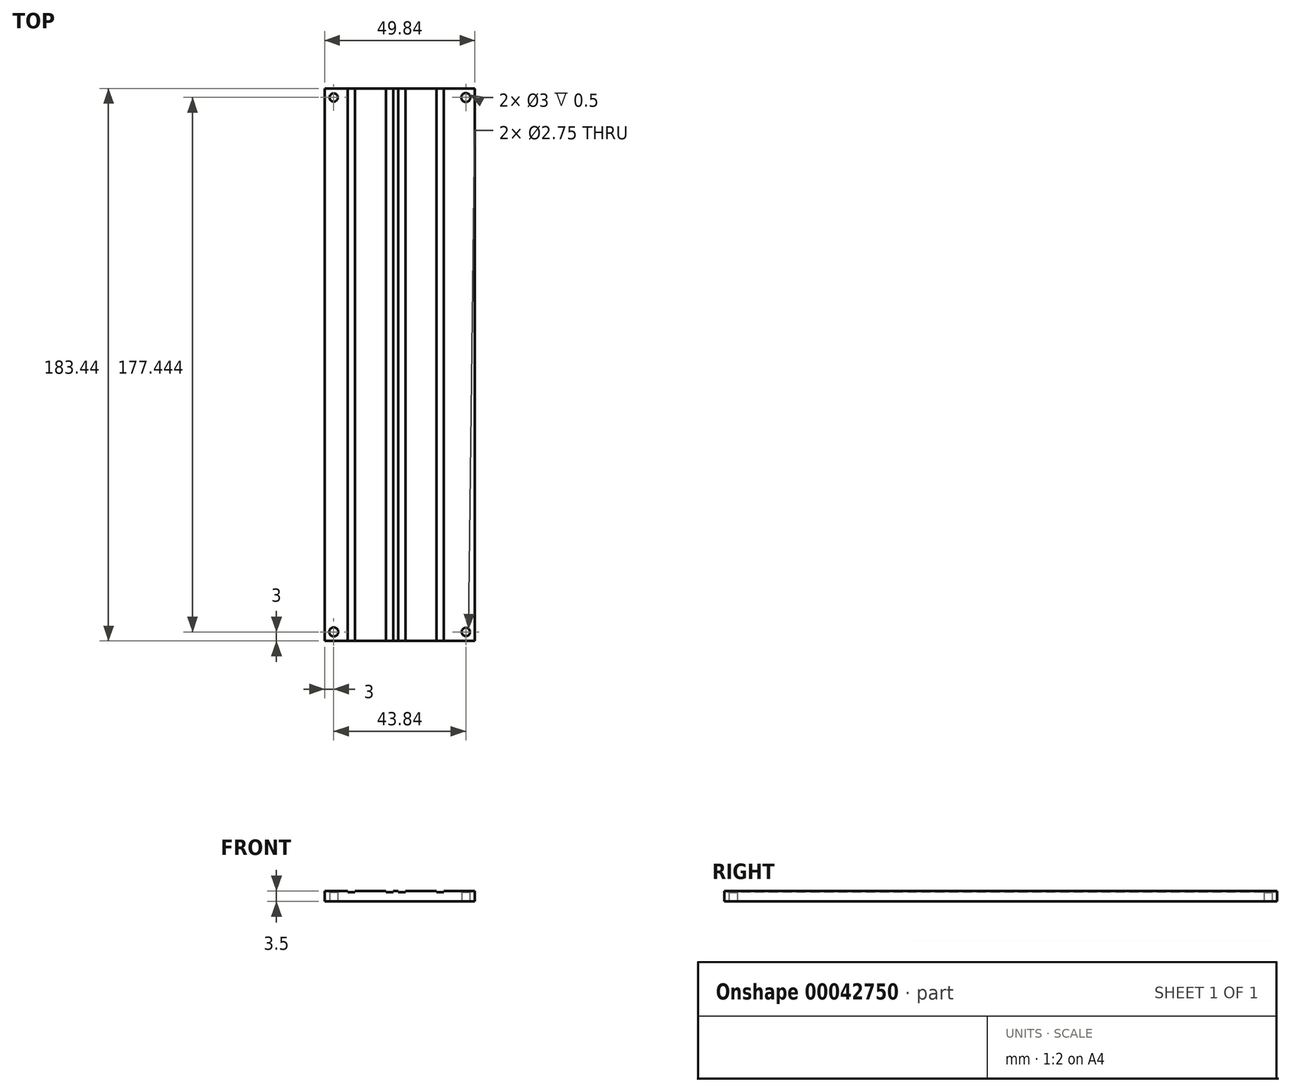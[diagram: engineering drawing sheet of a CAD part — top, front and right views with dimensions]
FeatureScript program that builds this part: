
annotation { "Feature Type Name" : "Feature", "Feature Type Description" : "" }
export const myFeature = defineFeature(function(context is Context, id is Id, definition is map)
    precondition{}
    {
        {
            var Q0;
            Q0=qCreatedBy(makeId("Top.planeOp"),FACE);
            var sketch = newSketch(context, id + "F0", { "sketchPlane" : qUnion([Q0])});
            skCircle(sketch, "E0", {"center": v(0, 0) * mm, "radius": 1.5 * mm});
            skCircle(sketch, "E1", {"center": v(43.84, 177.44) * mm, "radius": 1.5 * mm});
            skLineSegment(sketch, "E2.bottom", {"start": v(-3, 180.44) * mm, "end": v(46.84, 180.44) * mm});
            skLineSegment(sketch, "E2.top", {"start": v(-3, -3) * mm, "end": v(46.84, -3) * mm});
            skLineSegment(sketch, "E2.left", {"start": v(-3, 180.44) * mm, "end": v(-3, -3) * mm});
            skLineSegment(sketch, "E2.right", {"start": v(46.84, 180.44) * mm, "end": v(46.84, -3) * mm});
            skCircle(sketch, "E3", {"center": v(0, 177.44) * mm, "radius": 1.38 * mm});
            skCircle(sketch, "E4", {"center": v(43.84, 0) * mm, "radius": 1.38 * mm});
            skPoint(sketch, "E5.endSnap0", {"position": v(21.92, -3) * mm});
            skSolve(sketch);
        }
        {
            var Q0;
            Q0=makeQuery(id+"F0.imprint","IMPRINT",FACE,{"disambiguationData":[TD([[makeQuery(id+"F0.imprint","IMPRINT",EDGE,{"derivedFrom":sQuery(id+"F0.wireOp",EDGE,"E0")}),-1.0]])]});
            extrude(context, id + "F1", {"entities" : qUnion([Q0]), "depth" : .5 * mm});
        }
        {
            var Q0;
            Q0=makeQuery(id+"F1.opExtrude","CAP_FACE",FACE,{"disambiguationData":[OSD([sQuery(id+"F0.wireOp",EDGE,"E0"),sQuery(id+"F0.wireOp",EDGE,"E1"),sQuery(id+"F0.wireOp",EDGE,"E2.bottom"),sQuery(id+"F0.wireOp",EDGE,"E2.top"),sQuery(id+"F0.wireOp",EDGE,"E2.left"),sQuery(id+"F0.wireOp",EDGE,"E2.right"),sQuery(id+"F0.wireOp",EDGE,"e5278f3a-593b-43ce-a0b6-dc1b815632bb.rect.bottom"),sQuery(id+"F0.wireOp",EDGE,"e5278f3a-593b-43ce-a0b6-dc1b815632bb.rect.top"),sQuery(id+"F0.wireOp",EDGE,"e5278f3a-593b-43ce-a0b6-dc1b815632bb.rect.left"),sQuery(id+"F0.wireOp",EDGE,"e5278f3a-593b-43ce-a0b6-dc1b815632bb.rect.right"),sQuery(id+"F0.wireOp",EDGE,"0788b160-4dc1-422e-8e8c-0d42d97e9e21.rect.right"),sQuery(id+"F0.wireOp",EDGE,"0788b160-4dc1-422e-8e8c-0d42d97e9e21.rect.left"),sQuery(id+"F0.wireOp",EDGE,"0788b160-4dc1-422e-8e8c-0d42d97e9e21.rect.top"),sQuery(id+"F0.wireOp",EDGE,"0788b160-4dc1-422e-8e8c-0d42d97e9e21.rect.bottom"),sQuery(id+"F0.wireOp",EDGE,"9ae8423b-224c-4eed-8461-ac0ba12c67ef.rect.top"),sQuery(id+"F0.wireOp",EDGE,"9ae8423b-224c-4eed-8461-ac0ba12c67ef.rect.bottom"),sQuery(id+"F0.wireOp",EDGE,"9ae8423b-224c-4eed-8461-ac0ba12c67ef.rect.left"),sQuery(id+"F0.wireOp",EDGE,"9ae8423b-224c-4eed-8461-ac0ba12c67ef.rect.right"),sQuery(id+"F0.wireOp",EDGE,"511b1452-fdba-401d-9405-732c8af2f196.rect.top"),sQuery(id+"F0.wireOp",EDGE,"5224c5d0-f24c-45e1-9878-aebc782a1e99.rect.left"),sQuery(id+"F0.wireOp",EDGE,"511b1452-fdba-401d-9405-732c8af2f196.rect.bottom"),sQuery(id+"F0.wireOp",EDGE,"86b0135e-4755-4367-ae23-b1d375861a25.rect.top"),sQuery(id+"F0.wireOp",EDGE,"5224c5d0-f24c-45e1-9878-aebc782a1e99.rect.bottom"),sQuery(id+"F0.wireOp",EDGE,"5224c5d0-f24c-45e1-9878-aebc782a1e99.rect.top"),sQuery(id+"F0.wireOp",EDGE,"86b0135e-4755-4367-ae23-b1d375861a25.rect.bottom"),sQuery(id+"F0.wireOp",EDGE,"5224c5d0-f24c-45e1-9878-aebc782a1e99.rect.right"),sQuery(id+"F0.wireOp",EDGE,"86b0135e-4755-4367-ae23-b1d375861a25.rect.left"),sQuery(id+"F0.wireOp",EDGE,"86b0135e-4755-4367-ae23-b1d375861a25.rect.right"),sQuery(id+"F0.wireOp",EDGE,"511b1452-fdba-401d-9405-732c8af2f196.rect.right"),sQuery(id+"F0.wireOp",EDGE,"511b1452-fdba-401d-9405-732c8af2f196.rect.left"),sQuery(id+"F0.wireOp",EDGE,"b43a0ba4-9dba-46bc-968b-13e96fca23b3.rect.left"),sQuery(id+"F0.wireOp",EDGE,"b43a0ba4-9dba-46bc-968b-13e96fca23b3.rect.bottom"),sQuery(id+"F0.wireOp",EDGE,"7761b7ab-5946-4f6e-ad21-f6075cb1ff51.rect.top"),sQuery(id+"F0.wireOp",EDGE,"4726b28d-0386-4670-8967-bc6313adf6ef.rect.right"),sQuery(id+"F0.wireOp",EDGE,"7761b7ab-5946-4f6e-ad21-f6075cb1ff51.rect.right"),sQuery(id+"F0.wireOp",EDGE,"4726b28d-0386-4670-8967-bc6313adf6ef.rect.top"),sQuery(id+"F0.wireOp",EDGE,"b43a0ba4-9dba-46bc-968b-13e96fca23b3.rect.right"),sQuery(id+"F0.wireOp",EDGE,"4726b28d-0386-4670-8967-bc6313adf6ef.rect.bottom"),sQuery(id+"F0.wireOp",EDGE,"4726b28d-0386-4670-8967-bc6313adf6ef.rect.left"),sQuery(id+"F0.wireOp",EDGE,"7761b7ab-5946-4f6e-ad21-f6075cb1ff51.rect.left"),sQuery(id+"F0.wireOp",EDGE,"b43a0ba4-9dba-46bc-968b-13e96fca23b3.rect.top"),sQuery(id+"F0.wireOp",EDGE,"7761b7ab-5946-4f6e-ad21-f6075cb1ff51.rect.bottom"),sQuery(id+"F0.wireOp",EDGE,"57ca4f26-5c56-4c68-9457-4a64392f3347.rect.left"),sQuery(id+"F0.wireOp",EDGE,"0ff1be2a-a1a8-4b6e-9f00-62856e441f21.rect.right"),sQuery(id+"F0.wireOp",EDGE,"208a584b-ce05-4589-bfe7-39b1698a8194.rect.left"),sQuery(id+"F0.wireOp",EDGE,"3fd6ee33-8733-46eb-a767-dbbe76983c7d.rect.left"),sQuery(id+"F0.wireOp",EDGE,"7a9b5616-fe8a-4a4b-9298-42c4a7e55be2.rect.right"),sQuery(id+"F0.wireOp",EDGE,"04949f4e-e150-414f-b18a-4da78bc3358c.rect.right"),sQuery(id+"F0.wireOp",EDGE,"208a584b-ce05-4589-bfe7-39b1698a8194.rect.right"),sQuery(id+"F0.wireOp",EDGE,"7a9b5616-fe8a-4a4b-9298-42c4a7e55be2.rect.left"),sQuery(id+"F0.wireOp",EDGE,"3fd6ee33-8733-46eb-a767-dbbe76983c7d.rect.right"),sQuery(id+"F0.wireOp",EDGE,"04949f4e-e150-414f-b18a-4da78bc3358c.rect.left"),sQuery(id+"F0.wireOp",EDGE,"57ca4f26-5c56-4c68-9457-4a64392f3347.rect.right"),sQuery(id+"F0.wireOp",EDGE,"0ff1be2a-a1a8-4b6e-9f00-62856e441f21.rect.left"),sQuery(id+"F0.wireOp",EDGE,"04949f4e-e150-414f-b18a-4da78bc3358c.rect.top"),sQuery(id+"F0.wireOp",EDGE,"208a584b-ce05-4589-bfe7-39b1698a8194.rect.bottom"),sQuery(id+"F0.wireOp",EDGE,"7a9b5616-fe8a-4a4b-9298-42c4a7e55be2.rect.top"),sQuery(id+"F0.wireOp",EDGE,"208a584b-ce05-4589-bfe7-39b1698a8194.rect.top"),sQuery(id+"F0.wireOp",EDGE,"0ff1be2a-a1a8-4b6e-9f00-62856e441f21.rect.bottom"),sQuery(id+"F0.wireOp",EDGE,"7a9b5616-fe8a-4a4b-9298-42c4a7e55be2.rect.bottom"),sQuery(id+"F0.wireOp",EDGE,"0ff1be2a-a1a8-4b6e-9f00-62856e441f21.rect.top"),sQuery(id+"F0.wireOp",EDGE,"57ca4f26-5c56-4c68-9457-4a64392f3347.rect.top"),sQuery(id+"F0.wireOp",EDGE,"57ca4f26-5c56-4c68-9457-4a64392f3347.rect.bottom"),sQuery(id+"F0.wireOp",EDGE,"04949f4e-e150-414f-b18a-4da78bc3358c.rect.bottom"),sQuery(id+"F0.wireOp",EDGE,"3fd6ee33-8733-46eb-a767-dbbe76983c7d.rect.top"),sQuery(id+"F0.wireOp",EDGE,"3fd6ee33-8733-46eb-a767-dbbe76983c7d.rect.bottom"),sQuery(id+"F0.wireOp",EDGE,"e532b4a8-563d-4d6a-8b1a-a20fa318d2fc.rect.right"),sQuery(id+"F0.wireOp",EDGE,"70cd7b72-5c6a-41ce-aa97-58821a5495a2.rect.left"),sQuery(id+"F0.wireOp",EDGE,"c8e58609-f867-4bb0-9ef6-a67fd09ed313.rect.left"),sQuery(id+"F0.wireOp",EDGE,"7f84faf9-ebf7-483f-8f19-fe061d16c88f.rect.right"),sQuery(id+"F0.wireOp",EDGE,"7939643b-5da5-488a-aeaf-6eee9e5d4f94.rect.left"),sQuery(id+"F0.wireOp",EDGE,"32a260d1-513d-470c-9a95-00da4923ba82.rect.right"),sQuery(id+"F0.wireOp",EDGE,"88e53884-e192-42f0-bd1f-923dc15386a3.rect.right"),sQuery(id+"F0.wireOp",EDGE,"70cd7b72-5c6a-41ce-aa97-58821a5495a2.rect.right"),sQuery(id+"F0.wireOp",EDGE,"e532b4a8-563d-4d6a-8b1a-a20fa318d2fc.rect.left"),sQuery(id+"F0.wireOp",EDGE,"c8e58609-f867-4bb0-9ef6-a67fd09ed313.rect.right"),sQuery(id+"F0.wireOp",EDGE,"7f84faf9-ebf7-483f-8f19-fe061d16c88f.rect.left"),sQuery(id+"F0.wireOp",EDGE,"32a260d1-513d-470c-9a95-00da4923ba82.rect.left"),sQuery(id+"F0.wireOp",EDGE,"f61bf7cc-c32d-46f2-bc22-689eb20f4aa8.rect.right"),sQuery(id+"F0.wireOp",EDGE,"528fd60a-5173-460b-8718-95726cf1d0d3.rect.right"),sQuery(id+"F0.wireOp",EDGE,"7939643b-5da5-488a-aeaf-6eee9e5d4f94.rect.right"),sQuery(id+"F0.wireOp",EDGE,"88e53884-e192-42f0-bd1f-923dc15386a3.rect.left"),sQuery(id+"F0.wireOp",EDGE,"f61bf7cc-c32d-46f2-bc22-689eb20f4aa8.rect.left"),sQuery(id+"F0.wireOp",EDGE,"528fd60a-5173-460b-8718-95726cf1d0d3.rect.left"),sQuery(id+"F0.wireOp",EDGE,"601dbf1e-1562-48c8-971d-08c2e95b1b61.rect.left"),sQuery(id+"F0.wireOp",EDGE,"c8e58609-f867-4bb0-9ef6-a67fd09ed313.rect.bottom"),sQuery(id+"F0.wireOp",EDGE,"88e53884-e192-42f0-bd1f-923dc15386a3.rect.top"),sQuery(id+"F0.wireOp",EDGE,"70cd7b72-5c6a-41ce-aa97-58821a5495a2.rect.bottom"),sQuery(id+"F0.wireOp",EDGE,"75fc349b-8e82-414b-b9d7-0717b741608d.rect.right"),sQuery(id+"F0.wireOp",EDGE,"2ff48f1a-e787-4175-bc96-8065b9f0d86f.rect.top"),sQuery(id+"F0.wireOp",EDGE,"75fc349b-8e82-414b-b9d7-0717b741608d.rect.bottom"),sQuery(id+"F0.wireOp",EDGE,"2ff48f1a-e787-4175-bc96-8065b9f0d86f.rect.left"),sQuery(id+"F0.wireOp",EDGE,"2ff48f1a-e787-4175-bc96-8065b9f0d86f.rect.bottom"),sQuery(id+"F0.wireOp",EDGE,"32a260d1-513d-470c-9a95-00da4923ba82.rect.bottom"),sQuery(id+"F0.wireOp",EDGE,"88e53884-e192-42f0-bd1f-923dc15386a3.rect.bottom"),sQuery(id+"F0.wireOp",EDGE,"528fd60a-5173-460b-8718-95726cf1d0d3.rect.top"),sQuery(id+"F0.wireOp",EDGE,"f61bf7cc-c32d-46f2-bc22-689eb20f4aa8.rect.bottom"),sQuery(id+"F0.wireOp",EDGE,"601dbf1e-1562-48c8-971d-08c2e95b1b61.rect.right"),sQuery(id+"F0.wireOp",EDGE,"7f84faf9-ebf7-483f-8f19-fe061d16c88f.rect.top"),sQuery(id+"F0.wireOp",EDGE,"601dbf1e-1562-48c8-971d-08c2e95b1b61.rect.bottom"),sQuery(id+"F0.wireOp",EDGE,"528fd60a-5173-460b-8718-95726cf1d0d3.rect.bottom"),sQuery(id+"F0.wireOp",EDGE,"e532b4a8-563d-4d6a-8b1a-a20fa318d2fc.rect.top"),sQuery(id+"F0.wireOp",EDGE,"75fc349b-8e82-414b-b9d7-0717b741608d.rect.top"),sQuery(id+"F0.wireOp",EDGE,"601dbf1e-1562-48c8-971d-08c2e95b1b61.rect.top"),sQuery(id+"F0.wireOp",EDGE,"32a260d1-513d-470c-9a95-00da4923ba82.rect.top"),sQuery(id+"F0.wireOp",EDGE,"f61bf7cc-c32d-46f2-bc22-689eb20f4aa8.rect.top"),sQuery(id+"F0.wireOp",EDGE,"7f84faf9-ebf7-483f-8f19-fe061d16c88f.rect.bottom"),sQuery(id+"F0.wireOp",EDGE,"e532b4a8-563d-4d6a-8b1a-a20fa318d2fc.rect.bottom"),sQuery(id+"F0.wireOp",EDGE,"70cd7b72-5c6a-41ce-aa97-58821a5495a2.rect.top"),sQuery(id+"F0.wireOp",EDGE,"75fc349b-8e82-414b-b9d7-0717b741608d.rect.left"),sQuery(id+"F0.wireOp",EDGE,"7939643b-5da5-488a-aeaf-6eee9e5d4f94.rect.bottom"),sQuery(id+"F0.wireOp",EDGE,"7939643b-5da5-488a-aeaf-6eee9e5d4f94.rect.top"),sQuery(id+"F0.wireOp",EDGE,"c8e58609-f867-4bb0-9ef6-a67fd09ed313.rect.top"),sQuery(id+"F0.wireOp",EDGE,"2ff48f1a-e787-4175-bc96-8065b9f0d86f.rect.right"),sQuery(id+"F0.wireOp",EDGE,"34bcf3fd-ed4a-4185-adf8-dc405735c649.rect.left"),sQuery(id+"F0.wireOp",EDGE,"e34a8003-39e3-4020-9972-05b17e0e0dd2.rect.right"),sQuery(id+"F0.wireOp",EDGE,"5d584f02-6df5-43d9-a6c0-44b15491b2ef.rect.right"),sQuery(id+"F0.wireOp",EDGE,"5d584f02-6df5-43d9-a6c0-44b15491b2ef.rect.left"),sQuery(id+"F0.wireOp",EDGE,"34bcf3fd-ed4a-4185-adf8-dc405735c649.rect.right"),sQuery(id+"F0.wireOp",EDGE,"e34a8003-39e3-4020-9972-05b17e0e0dd2.rect.left"),sQuery(id+"F0.wireOp",EDGE,"5d584f02-6df5-43d9-a6c0-44b15491b2ef.rect.bottom"),sQuery(id+"F0.wireOp",EDGE,"e34a8003-39e3-4020-9972-05b17e0e0dd2.rect.top"),sQuery(id+"F0.wireOp",EDGE,"e34a8003-39e3-4020-9972-05b17e0e0dd2.rect.bottom"),sQuery(id+"F0.wireOp",EDGE,"34bcf3fd-ed4a-4185-adf8-dc405735c649.rect.bottom"),sQuery(id+"F0.wireOp",EDGE,"34bcf3fd-ed4a-4185-adf8-dc405735c649.rect.top"),sQuery(id+"F0.wireOp",EDGE,"5d584f02-6df5-43d9-a6c0-44b15491b2ef.rect.top"),sQuery(id+"F0.wireOp",EDGE,"af60b362-f3e8-441e-9e1f-4259201feecf.rect.top"),sQuery(id+"F0.wireOp",EDGE,"f3d3602e-e124-40a7-96a1-dc4fa4adcf37.rect.bottom"),sQuery(id+"F0.wireOp",EDGE,"4a09bc43-db4a-4a7f-b510-9db42ac8ae9a.rect.top"),sQuery(id+"F0.wireOp",EDGE,"74e83cdb-cc94-4001-ac12-18727aacc957.rect.bottom"),sQuery(id+"F0.wireOp",EDGE,"242bfa70-7804-440d-99c3-28ec5b1ee65b.rect.left"),sQuery(id+"F0.wireOp",EDGE,"52d42c98-a837-46c3-ad31-eb32c8073d4f.rect.bottom"),sQuery(id+"F0.wireOp",EDGE,"af60b362-f3e8-441e-9e1f-4259201feecf.rect.left"),sQuery(id+"F0.wireOp",EDGE,"9a44f7b1-bce2-4215-bd6e-a2994b21c9db.rect.left"),sQuery(id+"F0.wireOp",EDGE,"9a44f7b1-bce2-4215-bd6e-a2994b21c9db.rect.top"),sQuery(id+"F0.wireOp",EDGE,"8898d686-7fb0-4204-8ff5-b49aa4418833.rect.bottom"),sQuery(id+"F0.wireOp",EDGE,"af60b362-f3e8-441e-9e1f-4259201feecf.rect.bottom"),sQuery(id+"F0.wireOp",EDGE,"47ae59bc-59bf-44a3-84ce-727988fe69e2.rect.top"),sQuery(id+"F0.wireOp",EDGE,"bc846ad1-a97c-4f09-9111-d1a515cad6f8.rect.bottom"),sQuery(id+"F0.wireOp",EDGE,"4a09bc43-db4a-4a7f-b510-9db42ac8ae9a.rect.right"),sQuery(id+"F0.wireOp",EDGE,"c0278d55-c928-4a3d-bbfd-8237f96a4b24.rect.top"),sQuery(id+"F0.wireOp",EDGE,"9a44f7b1-bce2-4215-bd6e-a2994b21c9db.rect.right"),sQuery(id+"F0.wireOp",EDGE,"c5aef39c-5632-48cf-8677-54e9030eb2c4.rect.bottom"),sQuery(id+"F0.wireOp",EDGE,"b62a0685-f6cc-45f3-8773-e225a674d48a.rect.bottom"),sQuery(id+"F0.wireOp",EDGE,"f09dc305-86ba-4384-8d9e-ed3973fdb031.rect.bottom"),sQuery(id+"F0.wireOp",EDGE,"2655523f-bddd-401e-8c3b-abefcb023dd8.rect.bottom"),sQuery(id+"F0.wireOp",EDGE,"b3a627d4-5a3a-4939-a623-0a0e6fe677c3.rect.top"),sQuery(id+"F0.wireOp",EDGE,"18b0f6b7-df90-4cf5-9876-91a50f2eee23.rect.top"),sQuery(id+"F0.wireOp",EDGE,"63a51c63-2273-4610-9e31-61f28d7edbfb.rect.top"),sQuery(id+"F0.wireOp",EDGE,"53dead6a-162f-43fe-8eb7-e704184291b4.rect.top"),sQuery(id+"F0.wireOp",EDGE,"c747e2a2-d4de-4c95-9238-e19881138373.rect.bottom"),sQuery(id+"F0.wireOp",EDGE,"118694ef-aa59-4623-b280-3f1e087cdfaa.rect.top"),sQuery(id+"F0.wireOp",EDGE,"360e989a-c57f-4c8e-90cd-6aefb2f6df26.rect.bottom"),sQuery(id+"F0.wireOp",EDGE,"9d1cec2a-90ec-449a-97f7-b9412bb1a96b.rect.right"),sQuery(id+"F0.wireOp",EDGE,"4a09bc43-db4a-4a7f-b510-9db42ac8ae9a.rect.left"),sQuery(id+"F0.wireOp",EDGE,"f3d3602e-e124-40a7-96a1-dc4fa4adcf37.rect.top"),sQuery(id+"F0.wireOp",EDGE,"f3d3602e-e124-40a7-96a1-dc4fa4adcf37.rect.left"),sQuery(id+"F0.wireOp",EDGE,"f3d3602e-e124-40a7-96a1-dc4fa4adcf37.rect.right"),sQuery(id+"F0.wireOp",EDGE,"ae8f8616-9d58-4ffb-8a16-d6d7847518c4.rect.top"),sQuery(id+"F0.wireOp",EDGE,"9d1cec2a-90ec-449a-97f7-b9412bb1a96b.rect.bottom"),sQuery(id+"F0.wireOp",EDGE,"f09dc305-86ba-4384-8d9e-ed3973fdb031.rect.left"),sQuery(id+"F0.wireOp",EDGE,"242bfa70-7804-440d-99c3-28ec5b1ee65b.rect.top"),sQuery(id+"F0.wireOp",EDGE,"f09dc305-86ba-4384-8d9e-ed3973fdb031.rect.right"),sQuery(id+"F0.wireOp",EDGE,"242bfa70-7804-440d-99c3-28ec5b1ee65b.rect.bottom"),sQuery(id+"F0.wireOp",EDGE,"58a05993-b02c-42f3-8c78-0aa3a8a034d9.rect.top"),sQuery(id+"F0.wireOp",EDGE,"9d1cec2a-90ec-449a-97f7-b9412bb1a96b.rect.left"),sQuery(id+"F0.wireOp",EDGE,"242bfa70-7804-440d-99c3-28ec5b1ee65b.rect.right"),sQuery(id+"F0.wireOp",EDGE,"af60b362-f3e8-441e-9e1f-4259201feecf.rect.right"),sQuery(id+"F0.wireOp",EDGE,"c747e2a2-d4de-4c95-9238-e19881138373.rect.left"),sQuery(id+"F0.wireOp",EDGE,"b62a0685-f6cc-45f3-8773-e225a674d48a.rect.top"),sQuery(id+"F0.wireOp",EDGE,"53dead6a-162f-43fe-8eb7-e704184291b4.rect.left"),sQuery(id+"F0.wireOp",EDGE,"360e989a-c57f-4c8e-90cd-6aefb2f6df26.rect.top"),sQuery(id+"F0.wireOp",EDGE,"2cb47c05-e519-4d57-b594-34d3ae56e2c8.rect.top"),sQuery(id+"F0.wireOp",EDGE,"118694ef-aa59-4623-b280-3f1e087cdfaa.rect.bottom"),sQuery(id+"F0.wireOp",EDGE,"bc846ad1-a97c-4f09-9111-d1a515cad6f8.rect.right"),sQuery(id+"F0.wireOp",EDGE,"435473e4-aa7a-485e-8a0a-2050a405410e.rect.bottom"),sQuery(id+"F0.wireOp",EDGE,"52d42c98-a837-46c3-ad31-eb32c8073d4f.rect.left"),sQuery(id+"F0.wireOp",EDGE,"63a51c63-2273-4610-9e31-61f28d7edbfb.rect.left"),sQuery(id+"F0.wireOp",EDGE,"4a09bc43-db4a-4a7f-b510-9db42ac8ae9a.rect.bottom"),sQuery(id+"F0.wireOp",EDGE,"ae8f8616-9d58-4ffb-8a16-d6d7847518c4.rect.right"),sQuery(id+"F0.wireOp",EDGE,"53dead6a-162f-43fe-8eb7-e704184291b4.rect.bottom"),sQuery(id+"F0.wireOp",EDGE,"bc846ad1-a97c-4f09-9111-d1a515cad6f8.rect.left"),sQuery(id+"F0.wireOp",EDGE,"74e83cdb-cc94-4001-ac12-18727aacc957.rect.right"),sQuery(id+"F0.wireOp",EDGE,"52d42c98-a837-46c3-ad31-eb32c8073d4f.rect.top"),sQuery(id+"F0.wireOp",EDGE,"435473e4-aa7a-485e-8a0a-2050a405410e.rect.top"),sQuery(id+"F0.wireOp",EDGE,"297ca8d3-144b-4ea2-a4cc-06fbe6e60c2f.rect.bottom"),sQuery(id+"F0.wireOp",EDGE,"118694ef-aa59-4623-b280-3f1e087cdfaa.rect.left"),sQuery(id+"F0.wireOp",EDGE,"c5aef39c-5632-48cf-8677-54e9030eb2c4.rect.top"),sQuery(id+"F0.wireOp",EDGE,"ae8f8616-9d58-4ffb-8a16-d6d7847518c4.rect.bottom"),sQuery(id+"F0.wireOp",EDGE,"bc846ad1-a97c-4f09-9111-d1a515cad6f8.rect.top"),sQuery(id+"F0.wireOp",EDGE,"74e83cdb-cc94-4001-ac12-18727aacc957.rect.left"),sQuery(id+"F0.wireOp",EDGE,"74e83cdb-cc94-4001-ac12-18727aacc957.rect.top"),sQuery(id+"F0.wireOp",EDGE,"297ca8d3-144b-4ea2-a4cc-06fbe6e60c2f.rect.left"),sQuery(id+"F0.wireOp",EDGE,"8898d686-7fb0-4204-8ff5-b49aa4418833.rect.top"),sQuery(id+"F0.wireOp",EDGE,"360e989a-c57f-4c8e-90cd-6aefb2f6df26.rect.left"),sQuery(id+"F0.wireOp",EDGE,"9a44f7b1-bce2-4215-bd6e-a2994b21c9db.rect.bottom"),sQuery(id+"F0.wireOp",EDGE,"47ae59bc-59bf-44a3-84ce-727988fe69e2.rect.bottom"),sQuery(id+"F0.wireOp",EDGE,"b3a627d4-5a3a-4939-a623-0a0e6fe677c3.rect.right"),sQuery(id+"F0.wireOp",EDGE,"435473e4-aa7a-485e-8a0a-2050a405410e.rect.right"),sQuery(id+"F0.wireOp",EDGE,"b62a0685-f6cc-45f3-8773-e225a674d48a.rect.right"),sQuery(id+"F0.wireOp",EDGE,"47ae59bc-59bf-44a3-84ce-727988fe69e2.rect.left"),sQuery(id+"F0.wireOp",EDGE,"c5aef39c-5632-48cf-8677-54e9030eb2c4.rect.right"),sQuery(id+"F0.wireOp",EDGE,"8898d686-7fb0-4204-8ff5-b49aa4418833.rect.right"),sQuery(id+"F0.wireOp",EDGE,"63a51c63-2273-4610-9e31-61f28d7edbfb.rect.bottom"),sQuery(id+"F0.wireOp",EDGE,"2655523f-bddd-401e-8c3b-abefcb023dd8.rect.right"),sQuery(id+"F0.wireOp",EDGE,"2655523f-bddd-401e-8c3b-abefcb023dd8.rect.left"),sQuery(id+"F0.wireOp",EDGE,"2655523f-bddd-401e-8c3b-abefcb023dd8.rect.top"),sQuery(id+"F0.wireOp",EDGE,"118694ef-aa59-4623-b280-3f1e087cdfaa.rect.right"),sQuery(id+"F0.wireOp",EDGE,"c747e2a2-d4de-4c95-9238-e19881138373.rect.top"),sQuery(id+"F0.wireOp",EDGE,"8898d686-7fb0-4204-8ff5-b49aa4418833.rect.left"),sQuery(id+"F0.wireOp",EDGE,"c5aef39c-5632-48cf-8677-54e9030eb2c4.rect.left"),sQuery(id+"F0.wireOp",EDGE,"297ca8d3-144b-4ea2-a4cc-06fbe6e60c2f.rect.right"),sQuery(id+"F0.wireOp",EDGE,"63a51c63-2273-4610-9e31-61f28d7edbfb.rect.right"),sQuery(id+"F0.wireOp",EDGE,"2cb47c05-e519-4d57-b594-34d3ae56e2c8.rect.right"),sQuery(id+"F0.wireOp",EDGE,"52d42c98-a837-46c3-ad31-eb32c8073d4f.rect.right"),sQuery(id+"F0.wireOp",EDGE,"b62a0685-f6cc-45f3-8773-e225a674d48a.rect.left"),sQuery(id+"F0.wireOp",EDGE,"b3a627d4-5a3a-4939-a623-0a0e6fe677c3.rect.left"),sQuery(id+"F0.wireOp",EDGE,"435473e4-aa7a-485e-8a0a-2050a405410e.rect.left"),sQuery(id+"F0.wireOp",EDGE,"297ca8d3-144b-4ea2-a4cc-06fbe6e60c2f.rect.top"),sQuery(id+"F0.wireOp",EDGE,"53dead6a-162f-43fe-8eb7-e704184291b4.rect.right"),sQuery(id+"F0.wireOp",EDGE,"2cb47c05-e519-4d57-b594-34d3ae56e2c8.rect.bottom"),sQuery(id+"F0.wireOp",EDGE,"2cb47c05-e519-4d57-b594-34d3ae56e2c8.rect.left"),sQuery(id+"F0.wireOp",EDGE,"ae8f8616-9d58-4ffb-8a16-d6d7847518c4.rect.left"),sQuery(id+"F0.wireOp",EDGE,"360e989a-c57f-4c8e-90cd-6aefb2f6df26.rect.right"),sQuery(id+"F0.wireOp",EDGE,"47ae59bc-59bf-44a3-84ce-727988fe69e2.rect.right"),sQuery(id+"F0.wireOp",EDGE,"b3a627d4-5a3a-4939-a623-0a0e6fe677c3.rect.bottom"),sQuery(id+"F0.wireOp",EDGE,"b5a73074-81ee-4659-be4a-df75b975c4ed.rect.top"),sQuery(id+"F0.wireOp",EDGE,"c747e2a2-d4de-4c95-9238-e19881138373.rect.right"),sQuery(id+"F0.wireOp",EDGE,"58a05993-b02c-42f3-8c78-0aa3a8a034d9.rect.left"),sQuery(id+"F0.wireOp",EDGE,"47dfa867-ac7e-48c2-bdf9-ba484dec7aad.rect.bottom"),sQuery(id+"F0.wireOp",EDGE,"b5a73074-81ee-4659-be4a-df75b975c4ed.rect.left"),sQuery(id+"F0.wireOp",EDGE,"47dfa867-ac7e-48c2-bdf9-ba484dec7aad.rect.top"),sQuery(id+"F0.wireOp",EDGE,"b5a73074-81ee-4659-be4a-df75b975c4ed.rect.bottom"),sQuery(id+"F0.wireOp",EDGE,"58a05993-b02c-42f3-8c78-0aa3a8a034d9.rect.right"),sQuery(id+"F0.wireOp",EDGE,"b5a73074-81ee-4659-be4a-df75b975c4ed.rect.right"),sQuery(id+"F0.wireOp",EDGE,"47dfa867-ac7e-48c2-bdf9-ba484dec7aad.rect.right"),sQuery(id+"F0.wireOp",EDGE,"18b0f6b7-df90-4cf5-9876-91a50f2eee23.rect.left"),sQuery(id+"F0.wireOp",EDGE,"f09dc305-86ba-4384-8d9e-ed3973fdb031.rect.top"),sQuery(id+"F0.wireOp",EDGE,"c0278d55-c928-4a3d-bbfd-8237f96a4b24.rect.right"),sQuery(id+"F0.wireOp",EDGE,"c0278d55-c928-4a3d-bbfd-8237f96a4b24.rect.bottom"),sQuery(id+"F0.wireOp",EDGE,"9d1cec2a-90ec-449a-97f7-b9412bb1a96b.rect.top"),sQuery(id+"F0.wireOp",EDGE,"18b0f6b7-df90-4cf5-9876-91a50f2eee23.rect.bottom"),sQuery(id+"F0.wireOp",EDGE,"18b0f6b7-df90-4cf5-9876-91a50f2eee23.rect.right"),sQuery(id+"F0.wireOp",EDGE,"c0278d55-c928-4a3d-bbfd-8237f96a4b24.rect.left"),sQuery(id+"F0.wireOp",EDGE,"47dfa867-ac7e-48c2-bdf9-ba484dec7aad.rect.left"),sQuery(id+"F0.wireOp",EDGE,"58a05993-b02c-42f3-8c78-0aa3a8a034d9.rect.bottom"),sQuery(id+"F0.wireOp",EDGE,"E3"),sQuery(id+"F0.wireOp",EDGE,"E4")])],"isStart":true});
            var sketch = newSketch(context, id + "F2", { "sketchPlane" : qUnion([Q0])});
            skLineSegment(sketch, "E6.bottom", {"start": v(-3, 3) * mm, "end": v(46.84, 3) * mm});
            skLineSegment(sketch, "E6.top", {"start": v(-3, -180.44) * mm, "end": v(46.84, -180.44) * mm});
            skLineSegment(sketch, "E6.left", {"start": v(-3, 3) * mm, "end": v(-3, -180.44) * mm});
            skLineSegment(sketch, "E6.right", {"start": v(46.84, 3) * mm, "end": v(46.84, -180.44) * mm});
            skCircle(sketch, "E7", {"center": v(43.84, 0) * mm, "radius": 1.38 * mm});
            skCircle(sketch, "E8", {"center": v(0, -177.44) * mm, "radius": 1.38 * mm});
            skSolve(sketch);
        }
        {
            var Q0;
            Q0=qSketchRegion(id+"F2",true);
            extrude(context, id + "F3", {"entities" : qUnion([Q0]), "operationType" : NewBodyOperationType.ADD, "depth" : 3 * mm});
        }
        {
            var Q0;
            Q0=makeQuery(id+"F1.opExtrude","CAP_FACE",FACE,{"disambiguationData":[OSD([sQuery(id+"F0.wireOp",EDGE,"E0"),sQuery(id+"F0.wireOp",EDGE,"E1"),sQuery(id+"F0.wireOp",EDGE,"E2.bottom"),sQuery(id+"F0.wireOp",EDGE,"E2.top"),sQuery(id+"F0.wireOp",EDGE,"E2.left"),sQuery(id+"F0.wireOp",EDGE,"E2.right"),sQuery(id+"F0.wireOp",EDGE,"E3"),sQuery(id+"F0.wireOp",EDGE,"E4")])],"isStart":false});
            var sketch = newSketch(context, id + "F4", { "sketchPlane" : qUnion([Q0])});
            skLineSegment(sketch, "E9.bottom", {"start": v(4.68, 180.44) * mm, "end": v(7.07, 180.44) * mm});
            skLineSegment(sketch, "E9.top", {"start": v(4.68, -3) * mm, "end": v(7.07, -3) * mm});
            skLineSegment(sketch, "E9.left", {"start": v(4.68, 180.44) * mm, "end": v(4.68, -3) * mm});
            skLineSegment(sketch, "E9.right", {"start": v(7.07, 180.44) * mm, "end": v(7.07, -3) * mm});
            skLineSegment(sketch, "E10.bottom", {"start": v(17.35, 180.44) * mm, "end": v(19.73, 180.44) * mm});
            skLineSegment(sketch, "E10.top", {"start": v(17.35, -3) * mm, "end": v(19.73, -3) * mm});
            skLineSegment(sketch, "E10.left", {"start": v(17.35, 180.44) * mm, "end": v(17.35, -3) * mm});
            skLineSegment(sketch, "E10.right", {"start": v(19.73, 180.44) * mm, "end": v(19.73, -3) * mm});
            skLineSegment(sketch, "E11.bottom", {"start": v(21.45, 180.44) * mm, "end": v(23.83, 180.44) * mm});
            skLineSegment(sketch, "E11.top", {"start": v(21.45, -3) * mm, "end": v(23.83, -3) * mm});
            skLineSegment(sketch, "E11.left", {"start": v(21.45, 180.44) * mm, "end": v(21.45, -3) * mm});
            skLineSegment(sketch, "E11.right", {"start": v(23.83, 180.44) * mm, "end": v(23.83, -3) * mm});
            skLineSegment(sketch, "E12.bottom", {"start": v(36.5, 180.44) * mm, "end": v(34.11, 180.44) * mm});
            skLineSegment(sketch, "E12.top", {"start": v(36.5, -3) * mm, "end": v(34.12, -3) * mm});
            skLineSegment(sketch, "E12.left", {"start": v(36.5, 180.44) * mm, "end": v(36.5, -3) * mm});
            skLineSegment(sketch, "E12.right", {"start": v(34.11, 180.44) * mm, "end": v(34.12, -3) * mm});
            skSolve(sketch);
        }
        {
            var Q0;
            Q0 = qSketchRegion(id + "F4", true);
            extrude(context, id + "F5", {"entities" : qUnion([Q0]), "operationType" : NewBodyOperationType.REMOVE, "oppositeDirection" : true, "depth" : .4 * mm});
        }
    });
